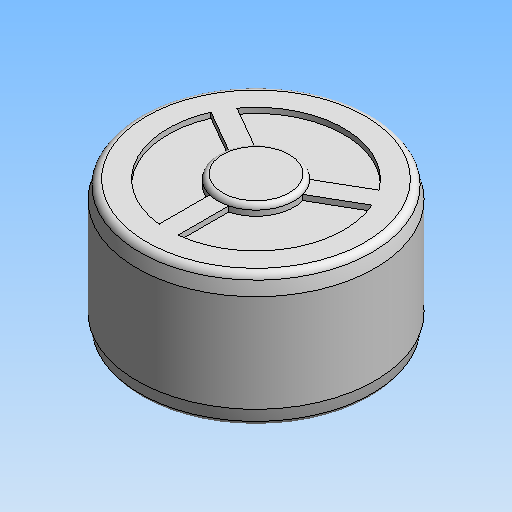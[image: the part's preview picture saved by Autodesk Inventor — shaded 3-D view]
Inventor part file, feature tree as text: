
AUTODESK INVENTOR PART (.ipt)
format: ipt  version: 2020 (Build 240168000, 168)  size: 177,152 bytes
history: native  units: mm (DEFAULTED — no unit token found)
features: other x7, sketch x2, revolve x1, extrude x1
ambient origin geometry x8: Origin, YZ Plane, XZ Plane, XY Plane, X Axis, Y Axis, Z Axis, Center Point
bodies: Solid1 (feature_tree)
feature tree (11):
  revolve  "Revolution1"  [1 undecoded]
  extrude  "Extrusion1"  [1 undecoded]
  other  "wheel_to_body_XY"
  other  "wheel_to_body_YZ"
  other  "wheel_to_body_ZX"
  other  "wheel_to_body_X"
  other  "wheel_to_body_Y"
  other  "wheel_to_body_Z"
  other  "wheel_to_body_Center"
  sketch  "Sketch_1"  dims[d0=360.0deg d1=28.0mm d2=0.0mm]
  sketch  "Sketch_5"
note: 2 required parameter values undecoded (feature->parameter linkage not recoverable at this tier; creation-order binding heuristic only, values carry confidence <= 0.55)